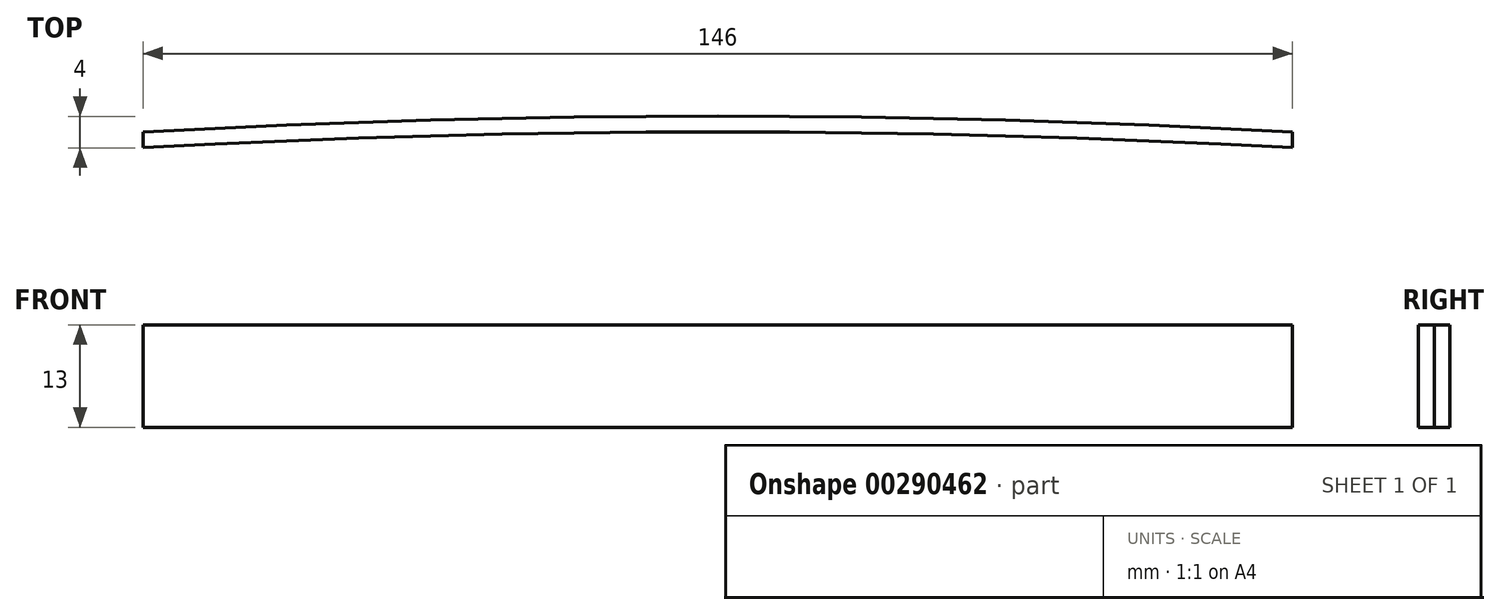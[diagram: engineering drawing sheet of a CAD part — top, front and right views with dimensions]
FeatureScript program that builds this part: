
annotation { "Feature Type Name" : "Feature", "Feature Type Description" : "" }
export const myFeature = defineFeature(function(context is Context, id is Id, definition is map)
    precondition{}
    {
        {
            var Q0;
            Q0=qCreatedBy(makeId("Top.planeOp"),FACE);
            var sketch = newSketch(context, id + "F0", { "sketchPlane" : qUnion([Q0])});
            skArc(sketch, "E0", {"start": v(72.46, 6.93) * mm, "mid": v(-0.54, 8.93) * mm, "end": v(-73.54, 6.93) * mm});
            skLineSegment(sketch, "E1", {"start": v(-73.54, 6.93) * mm, "end": v(-73.54, 4.93) * mm});
            skLineSegment(sketch, "E2", {"start": v(72.46, 6.93) * mm, "end": v(72.46, 4.93) * mm});
            skArc(sketch, "E3", {"start": v(72.46, 4.93) * mm, "mid": v(-0.54, 6.93) * mm, "end": v(-73.54, 4.93) * mm});
            skLineSegment(sketch, "E4", {"start": v(-73.54, 4.93) * mm, "end": v(72.46, 4.93) * mm, "construction": true});
            skSolve(sketch);
        }
        {
            var Q0;
            Q0=qSketchRegion(id+"F0",true);
            extrude(context, id + "F1", {"entities" : qUnion([Q0]), "depth" : 13 * mm});
        }
    });
